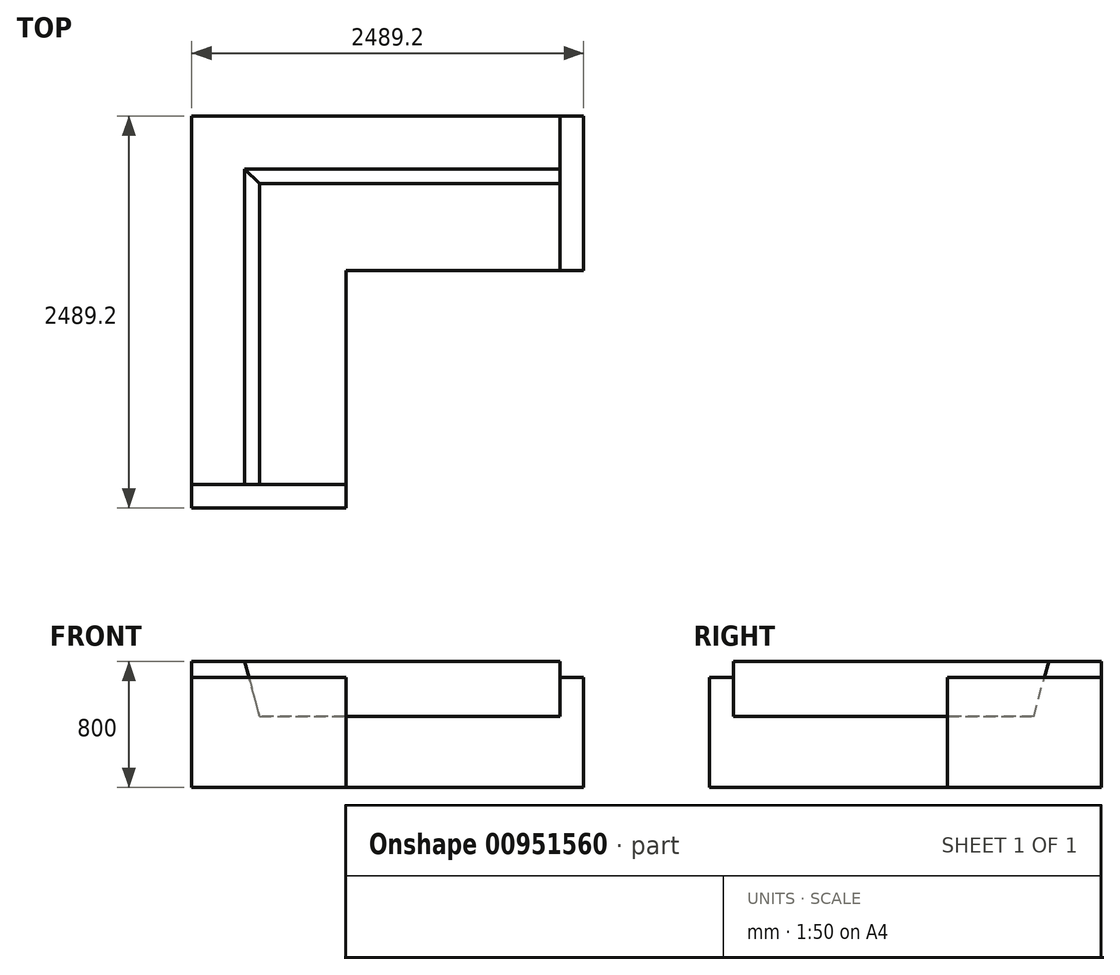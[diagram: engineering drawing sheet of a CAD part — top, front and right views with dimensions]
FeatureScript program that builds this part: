
annotation { "Feature Type Name" : "Feature", "Feature Type Description" : "" }
export const myFeature = defineFeature(function(context is Context, id is Id, definition is map)
    precondition{}
    {
        {
            var Q0;
            Q0=qCreatedBy(makeId("Top.planeOp"),FACE);
            var sketch = newSketch(context, id + "F0", { "sketchPlane" : qUnion([Q0])});
            skLineSegment(sketch, "E0", {"start": v(0, 0) * mm, "end": v(0, 2489.2) * mm});
            skLineSegment(sketch, "E1", {"start": v(0, 2489.2) * mm, "end": v(2489.2, 2489.2) * mm});
            skLineSegment(sketch, "E2", {"start": v(0, 0) * mm, "end": v(980, 0) * mm});
            skLineSegment(sketch, "E3", {"start": v(2489.2, 2489.2) * mm, "end": v(2489.2, 1509.2) * mm});
            skLineSegment(sketch, "E4", {"start": v(980, 0) * mm, "end": v(980, 1509.2) * mm});
            skLineSegment(sketch, "E5", {"start": v(980, 1509.2) * mm, "end": v(2489.2, 1509.2) * mm});
            skSolve(sketch);
        }
        {
            var Q0;
            Q0 = qSketchRegion(id + "F0", true);
            extrude(context, id + "F1", {"entities" : qUnion([Q0]), "depth" : 450 * mm, "offsetDistance" : 25.4 * mm});
        }
        {
            var Q0;
            Q0=makeQuery(id+"F1.opExtrude","CAP_FACE",FACE,{"disambiguationData":[OSD([sQuery(id+"F0.wireOp",EDGE,"E0"),sQuery(id+"F0.wireOp",EDGE,"E1"),sQuery(id+"F0.wireOp",EDGE,"E2"),sQuery(id+"F0.wireOp",EDGE,"E3"),sQuery(id+"F0.wireOp",EDGE,"E4"),sQuery(id+"F0.wireOp",EDGE,"E5")])],"isStart":false});
            var sketch = newSketch(context, id + "F2", { "sketchPlane" : qUnion([Q0])});
            skLineSegment(sketch, "E6.bottom", {"start": v(980, 0) * mm, "end": v(0, 0) * mm});
            skLineSegment(sketch, "E6.top", {"start": v(980, 150) * mm, "end": v(0, 150) * mm});
            skLineSegment(sketch, "E6.left", {"start": v(980, 0) * mm, "end": v(980, 150) * mm});
            skLineSegment(sketch, "E6.right", {"start": v(0, 0) * mm, "end": v(0, 150) * mm});
            skLineSegment(sketch, "E7.bottom", {"start": v(2489.2, 1509.2) * mm, "end": v(2339.2, 1509.2) * mm});
            skLineSegment(sketch, "E7.top", {"start": v(2489.2, 2489.2) * mm, "end": v(2339.2, 2489.2) * mm});
            skLineSegment(sketch, "E7.left", {"start": v(2489.2, 1509.2) * mm, "end": v(2489.2, 2489.2) * mm});
            skLineSegment(sketch, "E7.right", {"start": v(2339.2, 1509.2) * mm, "end": v(2339.2, 2489.2) * mm});
            skSolve(sketch);
        }
        {
            var Q0;
            Q0 = qSketchRegion(id + "F2", true);
            extrude(context, id + "F3", {"entities" : qUnion([Q0]), "operationType" : NewBodyOperationType.ADD, "depth" : 700 * mm - 450 * mm, "offsetDistance" : 25.4 * mm});
        }
        {
            var Q0;
            Q0=makeQuery(id+"F3.opExtrude","SWEPT_FACE",FACE,{"disambiguationData":[OSD([sQuery(id+"F2.wireOp",EDGE,"E6.top")])]});
            var sketch = newSketch(context, id + "F4", { "sketchPlane" : qUnion([Q0])});
            skLineSegment(sketch, "E8", {"start": v(0, 450) * mm, "end": v(0, 800) * mm});
            skLineSegment(sketch, "E9", {"start": v(0, 800) * mm, "end": v(-336.22, 800) * mm});
            skLineSegment(sketch, "E10", {"start": v(-336.22, 800) * mm, "end": v(-430, 450) * mm});
            skLineSegment(sketch, "E11", {"start": v(-430, 450) * mm, "end": v(0, 450) * mm});
            skSolve(sketch);
        }
        {
            var Q0;
            Q0 = qSketchRegion(id + "F4", true);
            var Q1;
            Q1=makeQuery(id+"F3.boolean.opBoolean","MERGE",FACE,{"derivedFrom":[makeQuery(id+"F1.opExtrude","SWEPT_FACE",FACE,{"disambiguationData":[OSD([sQuery(id+"F0.wireOp",EDGE,"E1")])]}),makeQuery(id+"F3.opExtrude","SWEPT_FACE",FACE,{"disambiguationData":[OSD([sQuery(id+"F2.wireOp",EDGE,"E7.top")])]})]});
            extrude(context, id + "F5", {"entities" : qUnion([Q0]), "operationType" : NewBodyOperationType.ADD, "endBound" : BoundingType.UP_TO_SURFACE, "depth" : 25.4 * mm, "endBoundEntityFace" : qUnion([Q1]), "offsetDistance" : 25.4 * mm});
        }
        {
            var Q0;
            Q0=makeQuery(id+"F3.opExtrude","SWEPT_FACE",FACE,{"disambiguationData":[OSD([sQuery(id+"F2.wireOp",EDGE,"E7.right")])]});
            var sketch = newSketch(context, id + "F6", { "sketchPlane" : qUnion([Q0])});
            skLineSegment(sketch, "E12", {"start": v(-2489.2, 450) * mm, "end": v(-2059.2, 450) * mm});
            skLineSegment(sketch, "E13", {"start": v(-2059.2, 450) * mm, "end": v(-2152.98, 800) * mm});
            skLineSegment(sketch, "E14", {"start": v(-2152.98, 800) * mm, "end": v(-2489.2, 800) * mm});
            skLineSegment(sketch, "E15", {"start": v(-2489.2, 800) * mm, "end": v(-2489.2, 450) * mm});
            skSolve(sketch);
        }
        {
            var Q0;
            Q0 = qSketchRegion(id + "F6", true);
            extrude(context, id + "F7", {"entities" : qUnion([Q0]), "operationType" : NewBodyOperationType.ADD, "endBound" : BoundingType.UP_TO_NEXT, "depth" : 25.4 * mm, "offsetDistance" : 25.4 * mm});
        }
    });
